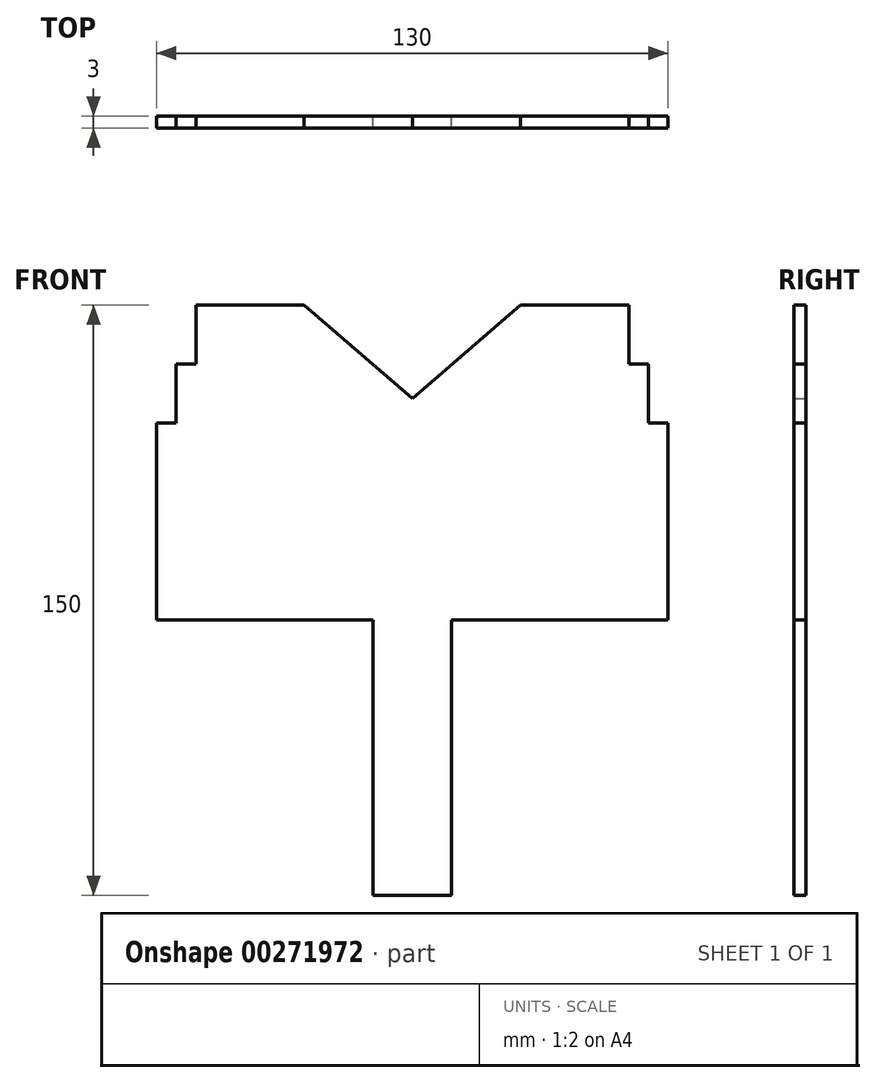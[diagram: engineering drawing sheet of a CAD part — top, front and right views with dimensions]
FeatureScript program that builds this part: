
annotation { "Feature Type Name" : "Feature", "Feature Type Description" : "" }
export const myFeature = defineFeature(function(context is Context, id is Id, definition is map)
    precondition{}
    {
        {
            var Q0;
            Q0=qCreatedBy(makeId("Front.planeOp"),FACE);
            var sketch = newSketch(context, id + "F0", { "sketchPlane" : qUnion([Q0])});
            skLineSegment(sketch, "E0", {"start": v(0, 0) * mm, "end": v(0, 150) * mm, "construction": true});
            skLineSegment(sketch, "E1", {"start": v(-55, 135) * mm, "end": v(-60, 135) * mm});
            skLineSegment(sketch, "E2", {"start": v(-60, 120) * mm, "end": v(-65, 120) * mm});
            skLineSegment(sketch, "E3", {"start": v(-55, 150) * mm, "end": v(-55, 135) * mm});
            skLineSegment(sketch, "E4", {"start": v(-60, 135) * mm, "end": v(-60, 120) * mm});
            skLineSegment(sketch, "E5", {"start": v(-65, 120) * mm, "end": v(-65, 70) * mm});
            skLineSegment(sketch, "E6", {"start": v(-65, 70) * mm, "end": v(-10, 70) * mm});
            skLineSegment(sketch, "E7", {"start": v(-27.5, 150) * mm, "end": v(0, 126.2) * mm});
            skCircle(sketch, "E8", {"center": v(0, 150) * mm, "radius": 18 * mm});
            skLineSegment(sketch, "E9.trimOffspring", {"start": v(-27.5, 150) * mm, "end": v(-55, 150) * mm});
            skCircle(sketch, "E10", {"center": v(0, 145.1) * mm, "radius": 14.3 * mm});
            skLineSegment(sketch, "E11", {"start": v(-10, 70) * mm, "end": v(-10, 0) * mm});
            skLineSegment(sketch, "E12", {"start": v(-10, 0) * mm, "end": v(0, 0) * mm});
            skLineSegment(sketch, "E13.MirrorCS", {"start": v(27.5, 150) * mm, "end": v(0, 126.2) * mm});
            skLineSegment(sketch, "E14.MirrorCS", {"start": v(27.5, 150) * mm, "end": v(55, 150) * mm});
            skLineSegment(sketch, "E15.MirrorCS", {"start": v(55, 150) * mm, "end": v(55, 135) * mm});
            skLineSegment(sketch, "E16.MirrorCS", {"start": v(55, 135) * mm, "end": v(60, 135) * mm});
            skLineSegment(sketch, "E17.MirrorCS", {"start": v(60, 120) * mm, "end": v(65, 120) * mm});
            skLineSegment(sketch, "E18.MirrorCS", {"start": v(60, 135) * mm, "end": v(60, 120) * mm});
            skLineSegment(sketch, "E19.MirrorCS", {"start": v(65, 120) * mm, "end": v(65, 70) * mm});
            skLineSegment(sketch, "E20.MirrorCS", {"start": v(65, 70) * mm, "end": v(10, 70) * mm});
            skLineSegment(sketch, "E21.MirrorCS", {"start": v(10, 0) * mm, "end": v(0, 0) * mm});
            skLineSegment(sketch, "E22.MirrorCS", {"start": v(10, 70) * mm, "end": v(10, 0) * mm});
            skSolve(sketch);
        }
        {
            var Q0;
            Q0=makeQuery(id+"F0.imprint","IMPRINT",FACE,{"disambiguationData":[TD([[makeQuery(id+"F0.imprint","IMPRINT",EDGE,{"derivedFrom":sQuery(id+"F0.wireOp",EDGE,"E1")}),1.0]])]});
            extrude(context, id + "F1", {"entities" : qUnion([Q0]), "depth" : 3 * mm});
        }
    });
